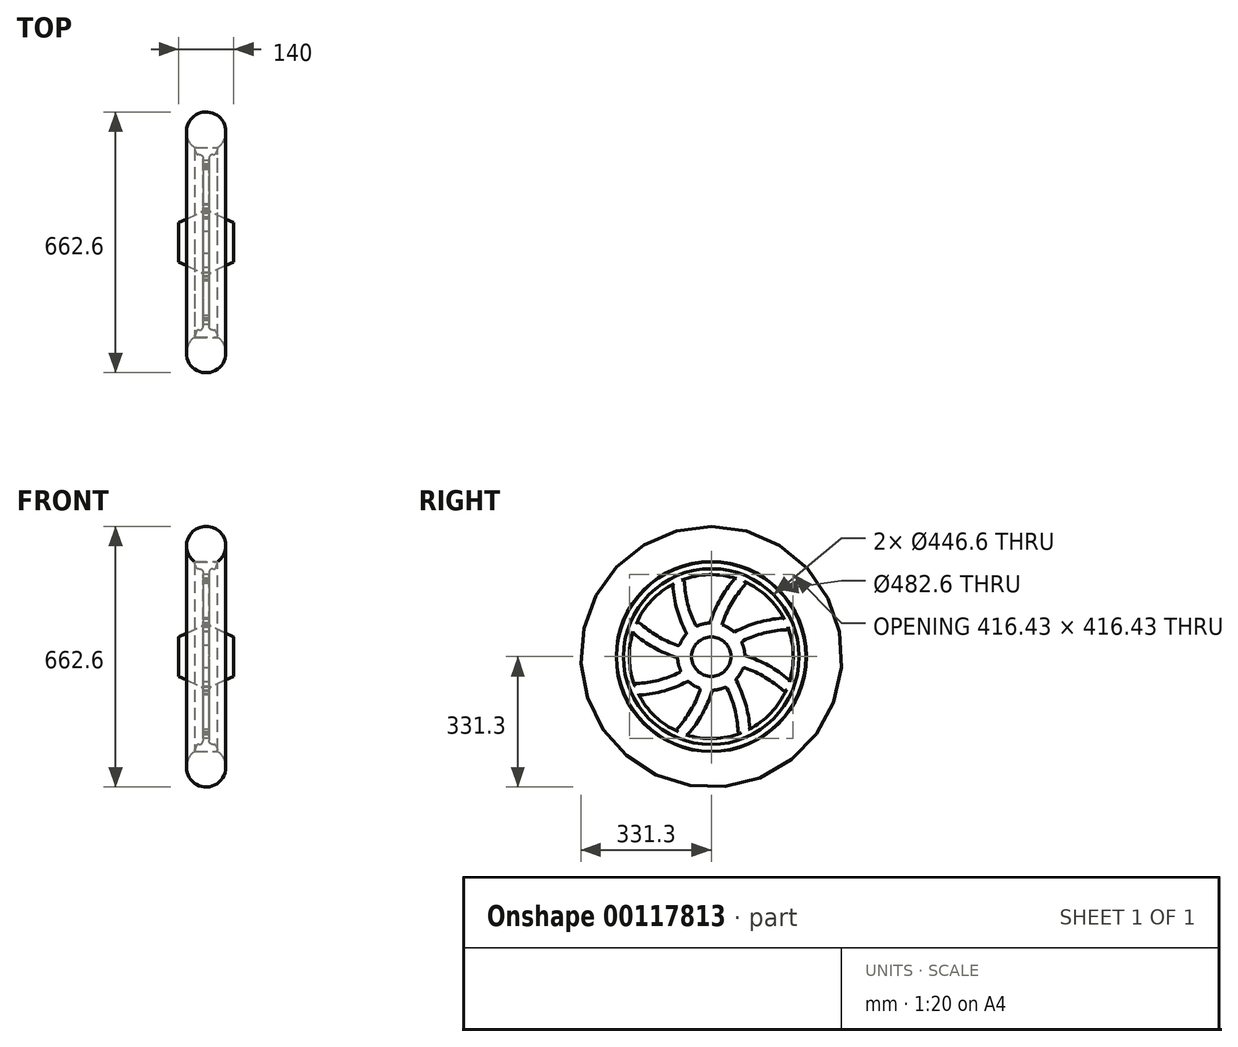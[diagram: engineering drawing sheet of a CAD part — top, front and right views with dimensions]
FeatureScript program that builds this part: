
annotation { "Feature Type Name" : "Feature", "Feature Type Description" : "" }
export const myFeature = defineFeature(function(context is Context, id is Id, definition is map)
    precondition{}
    {
        {
            var Q0;
            Q0=qCreatedBy(makeId("Front.planeOp"),FACE);
            var sketch = newSketch(context, id + "F0", { "sketchPlane" : qUnion([Q0])});
            skArc(sketch, "E0", {"start": v(0, 0) * mm, "mid": v(47.43, 34.19) * mm, "end": v(30, 90) * mm});
            skLineSegment(sketch, "E1", {"start": v(30, 90) * mm, "end": v(0, 90) * mm});
            skLineSegment(sketch, "E2", {"start": v(30, 91) * mm, "end": v(23.81, 108) * mm});
            skLineSegment(sketch, "E3", {"start": v(23.81, 108) * mm, "end": v(7.5, 108) * mm});
            skLineSegment(sketch, "E4", {"start": v(7.5, 108) * mm, "end": v(7.5, 252.16) * mm});
            skLineSegment(sketch, "E5", {"start": v(70, 331.3) * mm, "end": v(0, 331.3) * mm});
            skLineSegment(sketch, "E6", {"start": v(0, 331.3) * mm, "end": v(0, 0) * mm});
            skLineSegment(sketch, "E7", {"start": v(30, 90) * mm, "end": v(30, 91) * mm, "construction": true});
            skLineSegment(sketch, "E8", {"start": v(7.5, 252.16) * mm, "end": v(70, 281.3) * mm});
            skLineSegment(sketch, "E9", {"start": v(70, 281.3) * mm, "end": v(70, 331.3) * mm});
            skLineSegment(sketch, "E10", {"start": v(0, 91) * mm, "end": v(30, 91) * mm});
            skLineSegment(sketch, "E11", {"start": v(70, 281.3) * mm, "end": v(70, 0) * mm, "construction": true});
            skSolve(sketch);
        }
        {
            var Q0;
            Q0=makeQuery(id+"F0.imprint","IMPRINT",FACE,{"disambiguationData":[TD([[makeQuery(id+"F0.imprint","IMPRINT",EDGE,{"derivedFrom":sQuery(id+"F0.wireOp",EDGE,"E0")}),1.0]])]});
            var Q1;
            Q1=makeQuery(id+"F0.imprint","IMPRINT",FACE,{"disambiguationData":[TD([[makeQuery(id+"F0.imprint","IMPRINT",EDGE,{"derivedFrom":sQuery(id+"F0.wireOp",EDGE,"E2")}),1.0]])]});
            var Q2;
            Q2=sQuery(id+"F0.wireOp",EDGE,"E5");
            revolve(context, id + "F1", {"entities" : qUnion([Q0, Q1]), "axis" : qUnion([Q2]), "revolveType" : RevolveType.FULL});
        }
        {
            var Q0;
            Q0=makeQuery(id+"F1.opRevolve","SWEPT_FACE",FACE,{"disambiguationData":[OSD([sQuery(id+"F0.wireOp",EDGE,"E4")])]});
            fillet(context, id + "F2", {"entities" : qUnion([Q0]), "radius" : 10 * mm, "tangentPropagation" : true, "allowEdgeOverflow" : false});
        }
        {
            var Q0;
            Q0=makeQuery(id+"F1.opRevolve","SWEPT_EDGE",EDGE,{"disambiguationData":[OSD([sQuery(id+"F0.wireOp",EDGE,"E2"),sQuery(id+"F0.wireOp",EDGE,"E3")])]});
            var Q1;
            Q1=makeQuery(id+"F1.opRevolve","SWEPT_EDGE",EDGE,{"disambiguationData":[OSD([sQuery(id+"F0.wireOp",EDGE,"E2"),sQuery(id+"F0.wireOp",EDGE,"E10")])]});
            var Q2;
            Q2=makeQuery(id+"F1.opRevolve","SWEPT_EDGE",EDGE,{"disambiguationData":[OSD([sQuery(id+"F0.wireOp",EDGE,"E0"),sQuery(id+"F0.wireOp",EDGE,"E1")])]});
            fillet(context, id + "F3", {"entities" : qUnion([Q0, Q1, Q2]), "radius" : 3 * mm, "tangentPropagation" : true, "allowEdgeOverflow" : false});
        }
        {
            var Q0;
            Q0=qCreatedBy(makeId("Right.planeOp"),FACE);
            var sketch = newSketch(context, id + "F4", { "sketchPlane" : qUnion([Q0])});
            skCircle(sketch, "E12.0.0", {"center": v(0, 331.3) * mm, "radius": 50 * mm, "construction": true});
            skCircle(sketch, "E13.0", {"center": v(0, 331.3) * mm, "radius": 213.3 * mm, "construction": true});
            skArc(sketch, "E14.0", {"start": v(90.73, 518.8) * mm, "mid": v(75.95, 525.26) * mm, "end": v(60.73, 530.55) * mm});
            skLineSegment(sketch, "E15", {"start": v(0, 331.3) * mm, "end": v(285, 331.3) * mm, "construction": true});
            skArc(sketch, "E16", {"start": v(-2.57, 416.78) * mm, "mid": v(22.83, 477.14) * mm, "end": v(60.73, 530.55) * mm});
            skArc(sketch, "E17", {"start": v(27.43, 412.3) * mm, "mid": v(52.89, 469.23) * mm, "end": v(90.73, 518.8) * mm});
            skCircle(sketch, "E18", {"center": v(0, 331.3) * mm, "radius": 15 * mm, "construction": true});
            skArc(sketch, "E19.0", {"start": v(-2.57, 416.78) * mm, "mid": v(12.64, 415.88) * mm, "end": v(27.43, 412.3) * mm});
            skSolve(sketch);
        }
        {
            var Q0;
            Q0=qCreatedBy(makeId("Right.planeOp"),FACE);
            var sketch = newSketch(context, id + "F5", { "sketchPlane" : qUnion([Q0])});
            skCircle(sketch, "E20.0", {"center": v(0, 331.3) * mm, "radius": 213.3 * mm, "construction": true});
            skCircle(sketch, "E20.1", {"center": v(0, 331.3) * mm, "radius": 85.51 * mm});
            skCircle(sketch, "E21.0", {"center": v(0, 331.3) * mm, "radius": 208.3 * mm});
            skSolve(sketch);
        }
        {
            var Q0;
            Q0 = qSketchRegion(id + "F5", true);
            extrude(context, id + "F6", {"entities" : qUnion([Q0]), "operationType" : NewBodyOperationType.REMOVE, "endBound" : BoundingType.SYMMETRIC, "depth" : 50 * mm});
        }
        {
            var Q0;
            Q0=makeQuery(id+"F4.imprint","IMPRINT",FACE,{"disambiguationData":[TD([[makeQuery(id+"F4.imprint","IMPRINT",EDGE,{"derivedFrom":sQuery(id+"F4.wireOp",EDGE,"E14.0")}),1.0]])]});
            extrude(context, id + "F7", {"entities" : qUnion([Q0]), "depth" : 7.5 * mm});
        }
        {
            var Q0;
            Q0=makeQuery(id+"F7.opExtrude","SWEPT_BODY",BODY,{"disambiguationData":[OSD([sQuery(id+"F4.wireOp",EDGE,"E14.0"),sQuery(id+"F4.wireOp",EDGE,"E16"),sQuery(id+"F4.wireOp",EDGE,"E17"),sQuery(id+"F4.wireOp",EDGE,"E19.0")])]});
            var Q1;
            Q1=makeQuery(id+"F1.opRevolve","SWEPT_FACE",FACE,{"disambiguationData":[OSD([sQuery(id+"F0.wireOp",EDGE,"E8")])]});
            circularPattern(context, id + "F8", {"operationType" : NewBodyOperationType.ADD, "entities" : qUnion([Q0]), "axis" : qUnion([Q1]), "angle" : 45 * degree, "instanceCount" : 360 / 45});
        }
        {
            var Q0;
            Q0=makeQuery(id+"F8.opPattern","COPY",EDGE,{"derivedFrom":makeQuery(id+"F7.opExtrude","SWEPT_EDGE",EDGE,{"disambiguationData":[OSD([sQuery(id+"F4.wireOp",EDGE,"E14.0"),sQuery(id+"F4.wireOp",EDGE,"E16")])]}),"instanceName":"7"});
            var Q1;
            Q1=makeQuery(id+"F7.opExtrude","SWEPT_EDGE",EDGE,{"disambiguationData":[OSD([sQuery(id+"F4.wireOp",EDGE,"E14.0"),sQuery(id+"F4.wireOp",EDGE,"E16")])]});
            var Q2;
            Q2=makeQuery(id+"F8.opPattern","COPY",EDGE,{"derivedFrom":makeQuery(id+"F7.opExtrude","SWEPT_EDGE",EDGE,{"disambiguationData":[OSD([sQuery(id+"F4.wireOp",EDGE,"E14.0"),sQuery(id+"F4.wireOp",EDGE,"E17")])]}),"instanceName":"7"});
            var Q3;
            Q3=makeQuery(id+"F7.opExtrude","SWEPT_EDGE",EDGE,{"disambiguationData":[OSD([sQuery(id+"F4.wireOp",EDGE,"E14.0"),sQuery(id+"F4.wireOp",EDGE,"E17")])]});
            var Q4;
            Q4=makeQuery(id+"F8.opPattern","COPY",EDGE,{"derivedFrom":makeQuery(id+"F7.opExtrude","SWEPT_EDGE",EDGE,{"disambiguationData":[OSD([sQuery(id+"F4.wireOp",EDGE,"E14.0"),sQuery(id+"F4.wireOp",EDGE,"E16")])]}),"instanceName":"1"});
            var Q5;
            Q5=makeQuery(id+"F8.opPattern","COPY",EDGE,{"derivedFrom":makeQuery(id+"F7.opExtrude","SWEPT_EDGE",EDGE,{"disambiguationData":[OSD([sQuery(id+"F4.wireOp",EDGE,"E14.0"),sQuery(id+"F4.wireOp",EDGE,"E17")])]}),"instanceName":"1"});
            var Q6;
            Q6=makeQuery(id+"F8.opPattern","COPY",EDGE,{"derivedFrom":makeQuery(id+"F7.opExtrude","SWEPT_EDGE",EDGE,{"disambiguationData":[OSD([sQuery(id+"F4.wireOp",EDGE,"E14.0"),sQuery(id+"F4.wireOp",EDGE,"E16")])]}),"instanceName":"2"});
            var Q7;
            Q7=makeQuery(id+"F8.opPattern","COPY",EDGE,{"derivedFrom":makeQuery(id+"F7.opExtrude","SWEPT_EDGE",EDGE,{"disambiguationData":[OSD([sQuery(id+"F4.wireOp",EDGE,"E14.0"),sQuery(id+"F4.wireOp",EDGE,"E17")])]}),"instanceName":"2"});
            var Q8;
            Q8=makeQuery(id+"F8.opPattern","COPY",EDGE,{"derivedFrom":makeQuery(id+"F7.opExtrude","SWEPT_EDGE",EDGE,{"disambiguationData":[OSD([sQuery(id+"F4.wireOp",EDGE,"E14.0"),sQuery(id+"F4.wireOp",EDGE,"E16")])]}),"instanceName":"3"});
            var Q9;
            Q9=makeQuery(id+"F8.opPattern","COPY",EDGE,{"derivedFrom":makeQuery(id+"F7.opExtrude","SWEPT_EDGE",EDGE,{"disambiguationData":[OSD([sQuery(id+"F4.wireOp",EDGE,"E14.0"),sQuery(id+"F4.wireOp",EDGE,"E17")])]}),"instanceName":"4"});
            var Q10;
            Q10=makeQuery(id+"F8.opPattern","COPY",EDGE,{"derivedFrom":makeQuery(id+"F7.opExtrude","SWEPT_EDGE",EDGE,{"disambiguationData":[OSD([sQuery(id+"F4.wireOp",EDGE,"E14.0"),sQuery(id+"F4.wireOp",EDGE,"E17")])]}),"instanceName":"3"});
            var Q11;
            Q11=makeQuery(id+"F8.opPattern","COPY",EDGE,{"derivedFrom":makeQuery(id+"F7.opExtrude","SWEPT_EDGE",EDGE,{"disambiguationData":[OSD([sQuery(id+"F4.wireOp",EDGE,"E14.0"),sQuery(id+"F4.wireOp",EDGE,"E16")])]}),"instanceName":"4"});
            var Q12;
            Q12=makeQuery(id+"F8.opPattern","COPY",EDGE,{"derivedFrom":makeQuery(id+"F7.opExtrude","SWEPT_EDGE",EDGE,{"disambiguationData":[OSD([sQuery(id+"F4.wireOp",EDGE,"E14.0"),sQuery(id+"F4.wireOp",EDGE,"E17")])]}),"instanceName":"5"});
            var Q13;
            Q13=makeQuery(id+"F8.opPattern","COPY",EDGE,{"derivedFrom":makeQuery(id+"F7.opExtrude","SWEPT_EDGE",EDGE,{"disambiguationData":[OSD([sQuery(id+"F4.wireOp",EDGE,"E14.0"),sQuery(id+"F4.wireOp",EDGE,"E16")])]}),"instanceName":"5"});
            var Q14;
            Q14=makeQuery(id+"F8.opPattern","COPY",EDGE,{"derivedFrom":makeQuery(id+"F7.opExtrude","SWEPT_EDGE",EDGE,{"disambiguationData":[OSD([sQuery(id+"F4.wireOp",EDGE,"E14.0"),sQuery(id+"F4.wireOp",EDGE,"E17")])]}),"instanceName":"6"});
            var Q15;
            Q15=makeQuery(id+"F8.opPattern","COPY",EDGE,{"derivedFrom":makeQuery(id+"F7.opExtrude","SWEPT_EDGE",EDGE,{"disambiguationData":[OSD([sQuery(id+"F4.wireOp",EDGE,"E14.0"),sQuery(id+"F4.wireOp",EDGE,"E16")])]}),"instanceName":"6"});
            var Q16;
            Q16=makeQuery(id+"F8.opPattern","COPY",EDGE,{"derivedFrom":makeQuery(id+"F7.opExtrude","SWEPT_EDGE",EDGE,{"disambiguationData":[OSD([sQuery(id+"F4.wireOp",EDGE,"E16"),sQuery(id+"F4.wireOp",EDGE,"E19.0")])]}),"instanceName":"1"});
            var Q17;
            Q17=makeQuery(id+"F8.opPattern","COPY",EDGE,{"derivedFrom":makeQuery(id+"F7.opExtrude","SWEPT_EDGE",EDGE,{"disambiguationData":[OSD([sQuery(id+"F4.wireOp",EDGE,"E17"),sQuery(id+"F4.wireOp",EDGE,"E19.0")])]}),"instanceName":"7"});
            var Q18;
            Q18=makeQuery(id+"F7.opExtrude","SWEPT_EDGE",EDGE,{"disambiguationData":[OSD([sQuery(id+"F4.wireOp",EDGE,"E17"),sQuery(id+"F4.wireOp",EDGE,"E19.0")])]});
            var Q19;
            Q19=makeQuery(id+"F8.opPattern","COPY",EDGE,{"derivedFrom":makeQuery(id+"F7.opExtrude","SWEPT_EDGE",EDGE,{"disambiguationData":[OSD([sQuery(id+"F4.wireOp",EDGE,"E17"),sQuery(id+"F4.wireOp",EDGE,"E19.0")])]}),"instanceName":"1"});
            var Q20;
            Q20=makeQuery(id+"F8.opPattern","COPY",EDGE,{"derivedFrom":makeQuery(id+"F7.opExtrude","SWEPT_EDGE",EDGE,{"disambiguationData":[OSD([sQuery(id+"F4.wireOp",EDGE,"E16"),sQuery(id+"F4.wireOp",EDGE,"E19.0")])]}),"instanceName":"2"});
            var Q21;
            Q21=makeQuery(id+"F8.opPattern","COPY",EDGE,{"derivedFrom":makeQuery(id+"F7.opExtrude","SWEPT_EDGE",EDGE,{"disambiguationData":[OSD([sQuery(id+"F4.wireOp",EDGE,"E16"),sQuery(id+"F4.wireOp",EDGE,"E19.0")])]}),"instanceName":"3"});
            var Q22;
            Q22=makeQuery(id+"F8.opPattern","COPY",EDGE,{"derivedFrom":makeQuery(id+"F7.opExtrude","SWEPT_EDGE",EDGE,{"disambiguationData":[OSD([sQuery(id+"F4.wireOp",EDGE,"E17"),sQuery(id+"F4.wireOp",EDGE,"E19.0")])]}),"instanceName":"2"});
            var Q23;
            Q23=makeQuery(id+"F8.opPattern","COPY",EDGE,{"derivedFrom":makeQuery(id+"F7.opExtrude","SWEPT_EDGE",EDGE,{"disambiguationData":[OSD([sQuery(id+"F4.wireOp",EDGE,"E17"),sQuery(id+"F4.wireOp",EDGE,"E19.0")])]}),"instanceName":"3"});
            var Q24;
            Q24=makeQuery(id+"F8.opPattern","COPY",EDGE,{"derivedFrom":makeQuery(id+"F7.opExtrude","SWEPT_EDGE",EDGE,{"disambiguationData":[OSD([sQuery(id+"F4.wireOp",EDGE,"E16"),sQuery(id+"F4.wireOp",EDGE,"E19.0")])]}),"instanceName":"4"});
            var Q25;
            Q25=makeQuery(id+"F8.opPattern","COPY",EDGE,{"derivedFrom":makeQuery(id+"F7.opExtrude","SWEPT_EDGE",EDGE,{"disambiguationData":[OSD([sQuery(id+"F4.wireOp",EDGE,"E17"),sQuery(id+"F4.wireOp",EDGE,"E19.0")])]}),"instanceName":"4"});
            var Q26;
            Q26=makeQuery(id+"F8.opPattern","COPY",EDGE,{"derivedFrom":makeQuery(id+"F7.opExtrude","SWEPT_EDGE",EDGE,{"disambiguationData":[OSD([sQuery(id+"F4.wireOp",EDGE,"E16"),sQuery(id+"F4.wireOp",EDGE,"E19.0")])]}),"instanceName":"5"});
            var Q27;
            Q27=makeQuery(id+"F8.opPattern","COPY",EDGE,{"derivedFrom":makeQuery(id+"F7.opExtrude","SWEPT_EDGE",EDGE,{"disambiguationData":[OSD([sQuery(id+"F4.wireOp",EDGE,"E17"),sQuery(id+"F4.wireOp",EDGE,"E19.0")])]}),"instanceName":"5"});
            var Q28;
            Q28=makeQuery(id+"F8.opPattern","COPY",EDGE,{"derivedFrom":makeQuery(id+"F7.opExtrude","SWEPT_EDGE",EDGE,{"disambiguationData":[OSD([sQuery(id+"F4.wireOp",EDGE,"E16"),sQuery(id+"F4.wireOp",EDGE,"E19.0")])]}),"instanceName":"6"});
            var Q29;
            Q29=makeQuery(id+"F8.opPattern","COPY",EDGE,{"derivedFrom":makeQuery(id+"F7.opExtrude","SWEPT_EDGE",EDGE,{"disambiguationData":[OSD([sQuery(id+"F4.wireOp",EDGE,"E17"),sQuery(id+"F4.wireOp",EDGE,"E19.0")])]}),"instanceName":"6"});
            var Q30;
            Q30=makeQuery(id+"F8.opPattern","COPY",EDGE,{"derivedFrom":makeQuery(id+"F7.opExtrude","SWEPT_EDGE",EDGE,{"disambiguationData":[OSD([sQuery(id+"F4.wireOp",EDGE,"E16"),sQuery(id+"F4.wireOp",EDGE,"E19.0")])]}),"instanceName":"7"});
            var Q31;
            Q31=makeQuery(id+"F7.opExtrude","SWEPT_EDGE",EDGE,{"disambiguationData":[OSD([sQuery(id+"F4.wireOp",EDGE,"E16"),sQuery(id+"F4.wireOp",EDGE,"E19.0")])]});
            fillet(context, id + "F9", {"entities" : qUnion([Q0, Q1, Q2, Q3, Q4, Q5, Q6, Q7, Q8, Q9, Q10, Q11, Q12, Q13, Q14, Q15, Q16, Q17, Q18, Q19, Q20, Q21, Q22, Q23, Q24, Q25, Q26, Q27, Q28, Q29, Q30, Q31]), "radius" : 5 * mm, "tangentPropagation" : true, "allowEdgeOverflow" : false});
        }
        {
            var Q0;
            Q0=makeQuery(id+"F6.boolean.opBoolean","SPLIT",BODY,{"disambiguationData":[OD(0.0)],"derivedFrom":makeQuery(id+"F1.opRevolve","SWEPT_BODY",BODY,{"disambiguationData":[OSD([sQuery(id+"F0.wireOp",EDGE,"E0"),sQuery(id+"F0.wireOp",EDGE,"E1"),sQuery(id+"F0.wireOp",EDGE,"E2"),sQuery(id+"F0.wireOp",EDGE,"E3"),sQuery(id+"F0.wireOp",EDGE,"E4"),sQuery(id+"F0.wireOp",EDGE,"E5"),sQuery(id+"F0.wireOp",EDGE,"E6"),sQuery(id+"F0.wireOp",EDGE,"E8"),sQuery(id+"F0.wireOp",EDGE,"E9"),sQuery(id+"F0.wireOp",EDGE,"5frkVusw-xOTp-UwYc-Iyrz-2meRA9PvLd1T"),sQuery(id+"F0.wireOp",EDGE,"E10")])]})});
            var Q1;
            Q1=makeQuery(id+"F1.opRevolve","SWEPT_BODY",BODY,{"disambiguationData":[OSD([sQuery(id+"F0.wireOp",EDGE,"E0"),sQuery(id+"F0.wireOp",EDGE,"E1"),sQuery(id+"F0.wireOp",EDGE,"E6")])]});
            var Q2;
            Q2=qCreatedBy(makeId("Right.planeOp"),FACE);
            mirror(context, id + "F10", {"operationType" : NewBodyOperationType.ADD, "entities" : qUnion([Q0, Q1]), "mirrorPlane" : qUnion([Q2])});
        }
    });
